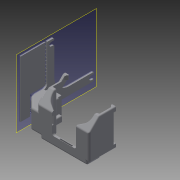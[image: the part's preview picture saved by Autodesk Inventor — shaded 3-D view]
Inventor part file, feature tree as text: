
AUTODESK INVENTOR PART (.ipt)
format: ipt  version: 2014 (Build 180170000, 170)  size: 1,247,744 bytes
history: native  units: in
note: dims shown in document units (in); Inventor stores cm internally (conversion verified against a paired STEP export)
features: extrude x8, sketch x8, fillet x5, other x1, plane x1, pattern_linear x1, imported_body x1
ambient origin geometry x8: Origin, YZ Plane, XZ Plane, XY Plane, X Axis, Y Axis, Z Axis, Center Point
bodies: Solid1 (feature_tree)
feature tree (25):
  other  "uploads-a6-b2-57-75-86-ReplicatorFanDuct21"
  extrude  "Extrusion1"  Depth=0.1in TaperAngle=0.0deg
  fillet  "Fillet1"  Radius=0.1969in
  extrude  "Extrusion2"  Depth=0.1in
  fillet  "Fillet2"  Radius=0.1in
  extrude  "Extrusion4"  Depth=0.1575in
  fillet  "Fillet3"  Radius=1.5748in
  extrude  "Extrusion5"  Depth=0.0787in
  fillet  "Fillet4"  Radius=0.1575in
  fillet  "Fillet5"  Radius=0.0787in
  plane  "Work Plane1"
  extrude  "Extrusion7"  Depth=0.0787in
  extrude  "Extrusion8"  Depth=0.1969in
  pattern_linear  "Rectangular Pattern1"  Spacing1=0.0394in  [1 undecoded]
  extrude  "Extrusion9"  Depth=0.0591in
  extrude  "Extrusion10"  Depth=0.05in
  imported_body  "Base1"
  sketch  "Sketch1"  dims[d0=0.4331in d1=0.1in d2=0.0in d3=0.1969in]
  sketch  "Sketch2"  dims[d4=0.2756in d5=1.5748in d6=0.1in d7=0.0in]
  sketch  "Sketch4"  dims[d8=0.1575in d13=0.315in d14=1.5748in]
  sketch  "Sketch6"  dims[d15=0.1in d16=0.0in d17=0.5906in d19=0.1575in d20=0.0787in]
  sketch  "Sketch8"  dims[d21=0.0787in d22=0.0787in]
  sketch  "Sketch9"  dims[d23=0.1969in d24=0.1969in]
  sketch  "Sketch10"  dims[d25=0.1in d26=0.0in]
  sketch  "Sketch11"  dims[d27=0.0394in d28=0.0394in d34=0.0591in d35=0.0984in d36=0.0591in d37=0.05in d38=0.0in d39=0.05in d40=0.0in d41=4.7244in d43=0.126in d44=1.1811in d46=0.1181in d47=0.3937in d49=0.3937in d51=0.05in d52=0.0in d53=0.05in d54=0.0in]
note: 1 required parameter value undecoded (feature->parameter linkage not recoverable at this tier; creation-order binding heuristic only, values carry confidence <= 0.55)
